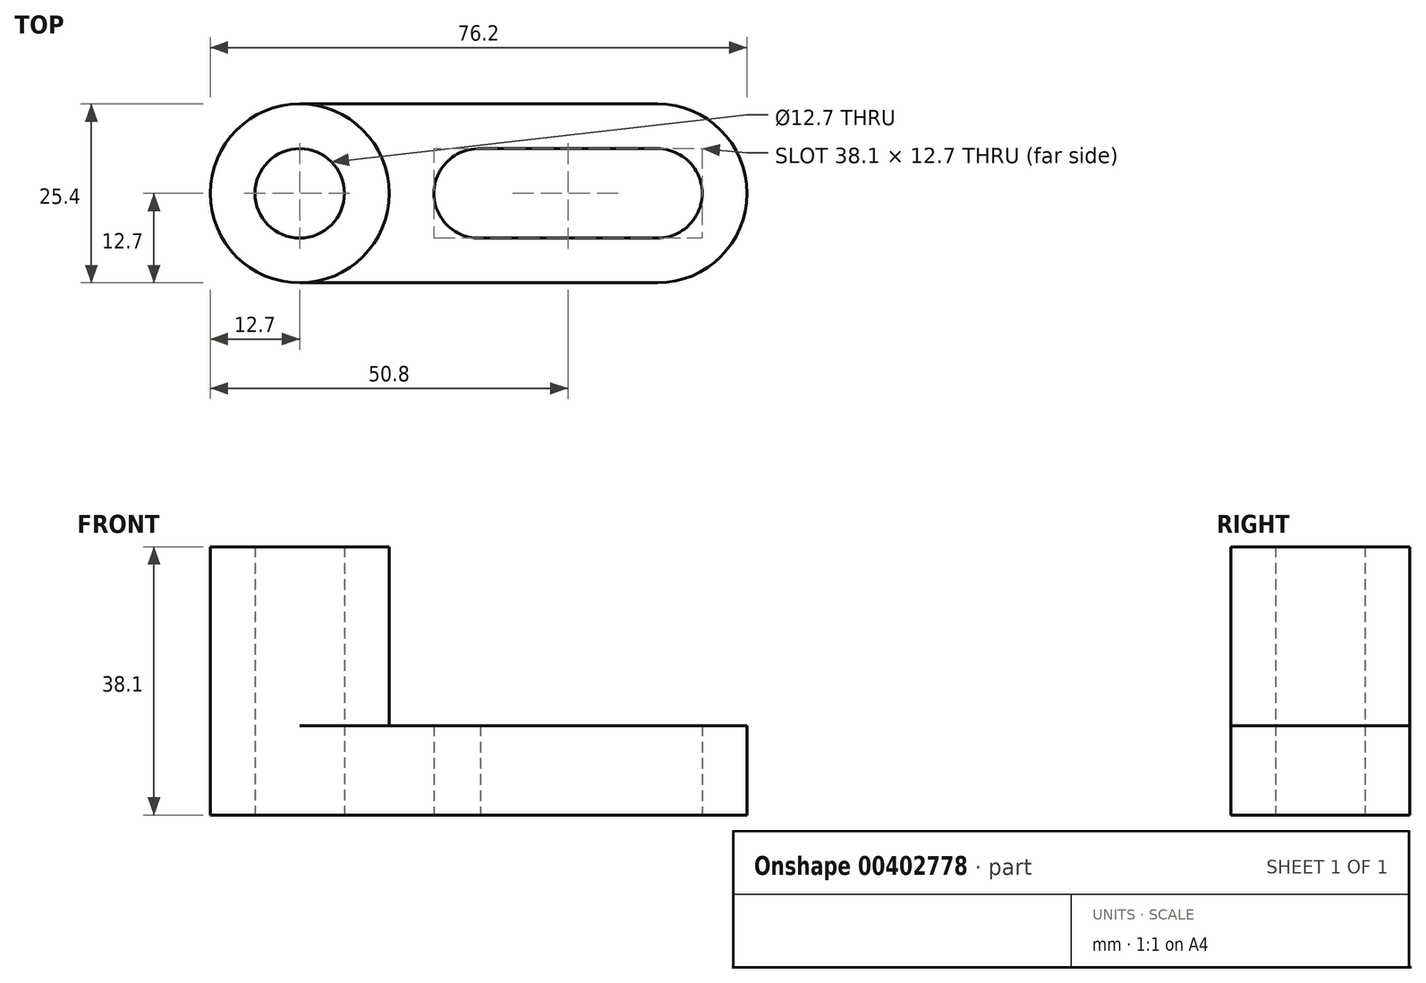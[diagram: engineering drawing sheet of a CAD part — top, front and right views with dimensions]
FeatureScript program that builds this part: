
annotation { "Feature Type Name" : "Feature", "Feature Type Description" : "" }
export const myFeature = defineFeature(function(context is Context, id is Id, definition is map)
    precondition{}
    {
        {
            var Q0;
            Q0=qCreatedBy(makeId("Top.planeOp"),FACE);
            var sketch = newSketch(context, id + "F0", { "sketchPlane" : qUnion([Q0])});
            skCircle(sketch, "E0", {"center": v(0, 0) * mm, "radius": 12.7 * mm});
            skCircle(sketch, "E1", {"center": v(0, 0) * mm, "radius": 6.35 * mm});
            skLineSegment(sketch, "E2", {"start": v(0, 0) * mm, "end": v(25.4, 0) * mm});
            skArc(sketch, "E3", {"start": v(25.66, 6.34) * mm, "mid": v(19.05, 0) * mm, "end": v(25.66, -6.34) * mm});
            skArc(sketch, "E4", {"start": v(50.8, -6.35) * mm, "mid": v(57.15, 0) * mm, "end": v(50.8, 6.35) * mm});
            skArc(sketch, "E5", {"start": v(50.8, -12.7) * mm, "mid": v(63.5, 0) * mm, "end": v(50.8, 12.7) * mm});
            skLineSegment(sketch, "E6", {"start": v(0, 12.7) * mm, "end": v(50.8, 12.7) * mm});
            skLineSegment(sketch, "E7", {"start": v(0, -12.7) * mm, "end": v(50.8, -12.7) * mm});
            skLineSegment(sketch, "E8", {"start": v(25.14, 6.34) * mm, "end": v(50.8, 6.35) * mm});
            skLineSegment(sketch, "E9", {"start": v(25.14, -6.34) * mm, "end": v(50.8, -6.35) * mm});
            skSolve(sketch);
        }
        {
            var Q0;
            Q0=makeQuery(id+"F0.imprint","IMPRINT",FACE,{"disambiguationData":[TD([[makeQuery(id+"F0.imprint","IMPRINT",EDGE,{"derivedFrom":sQuery(id+"F0.wireOp",EDGE,"E1")}),-1.0]])]});
            var Q1;
            {var subQ1=sQuery(id+"F0.wireOp",EDGE,"E4");Q1=makeQuery(id+"F0.imprint","IMPRINT",FACE,{"disambiguationData":[TD([[makeQuery(id+"F0.imprint","IMPRINT",EDGE,{"derivedFrom":subQ1}),-1.0]])]});}
            extrude(context, id + "F1", {"entities" : qUnion([Q0, Q1]), "depth" : 12.7 * mm});
        }
        {
            var Q0;
            Q0=makeQuery(id+"F1.opExtrude","CAP_FACE",FACE,{"disambiguationData":[OSD([sQuery(id+"F0.wireOp",EDGE,"E0"),sQuery(id+"F0.wireOp",EDGE,"E1"),sQuery(id+"F0.wireOp",EDGE,"E3"),sQuery(id+"F0.wireOp",EDGE,"E4"),sQuery(id+"F0.wireOp",EDGE,"E5"),sQuery(id+"F0.wireOp",EDGE,"E6"),sQuery(id+"F0.wireOp",EDGE,"E7"),sQuery(id+"F0.wireOp",EDGE,"E8"),sQuery(id+"F0.wireOp",EDGE,"E9")])],"isStart":false});
            var sketch = newSketch(context, id + "F2", { "sketchPlane" : qUnion([Q0])});
            skCircle(sketch, "E10", {"center": v(0, 0) * mm, "radius": 12.7 * mm});
            skSolve(sketch);
        }
        {
            var Q0;
            Q0=makeQuery(id+"F2.imprint","IMPRINT",FACE,{"disambiguationData":[TD([[makeQuery(id+"F2.imprint","IMPRINT",EDGE,{"derivedFrom":makeQuery(id+"F1.opExtrude","CAP_EDGE",EDGE,{"disambiguationData":[OSD([sQuery(id+"F0.wireOp",EDGE,"E1")])],"isStart":false})}),-1.0]])]});
            extrude(context, id + "F3", {"entities" : qUnion([Q0]), "operationType" : NewBodyOperationType.ADD, "depth" : 25.4 * mm});
        }
    });
